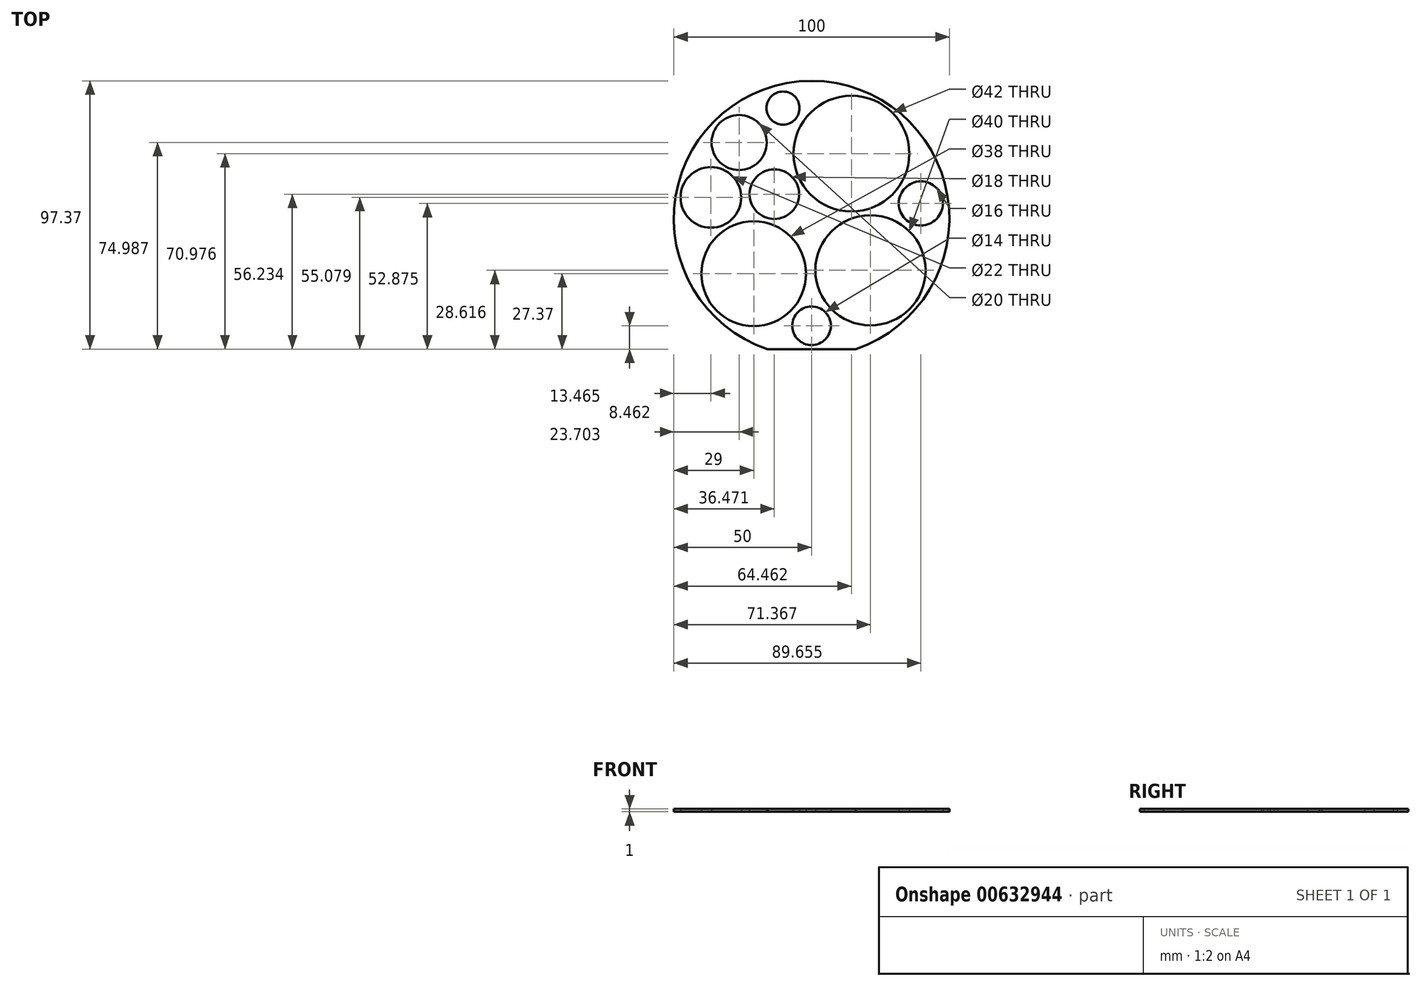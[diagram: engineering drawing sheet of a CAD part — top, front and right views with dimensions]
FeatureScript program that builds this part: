
annotation { "Feature Type Name" : "Feature", "Feature Type Description" : "" }
export const myFeature = defineFeature(function(context is Context, id is Id, definition is map)
    precondition{}
    {
        {
            var Q0;
            Q0=qCreatedBy(makeId("Top.planeOp"),FACE);
            var sketch = newSketch(context, id + "F0", { "sketchPlane" : qUnion([Q0])});
            skArc(sketch, "E0", {"start": v(16, -47.37) * mm, "mid": v(0, 50) * mm, "end": v(-16, -47.37) * mm});
            skLineSegment(sketch, "E1", {"start": v(-16, -47.37) * mm, "end": v(16, -47.37) * mm});
            skCircle(sketch, "E2", {"center": v(14.46, 23.6) * mm, "radius": 21 * mm});
            skCircle(sketch, "E3", {"center": v(21.37, -18.75) * mm, "radius": 20 * mm});
            skCircle(sketch, "E4", {"center": v(-21, -20) * mm, "radius": 19 * mm});
            skCircle(sketch, "E5", {"center": v(-13.53, 8.86) * mm, "radius": 9 * mm});
            skCircle(sketch, "E6", {"center": v(39.65, 5.5) * mm, "radius": 8 * mm});
            skCircle(sketch, "E7", {"center": v(-10.37, 40.13) * mm, "radius": 6 * mm});
            skCircle(sketch, "E8", {"center": v(0, -38.9) * mm, "radius": 7 * mm});
            skCircle(sketch, "E9", {"center": v(-36.53, 7.7) * mm, "radius": 11 * mm});
            skCircle(sketch, "E10", {"center": v(-26.3, 27.62) * mm, "radius": 10 * mm});
            skSolve(sketch);
        }
        {
            var Q0;
            Q0=makeQuery(id+"F0.imprint","IMPRINT",FACE,{"disambiguationData":[TD([[makeQuery(id+"F0.imprint","IMPRINT",EDGE,{"derivedFrom":sQuery(id+"F0.wireOp",EDGE,"E0")}),1.0]])]});
            extrude(context, id + "F1", {"entities" : qUnion([Q0]), "depth" : 1 * mm, "offsetDistance" : 25 * mm});
        }
    });
